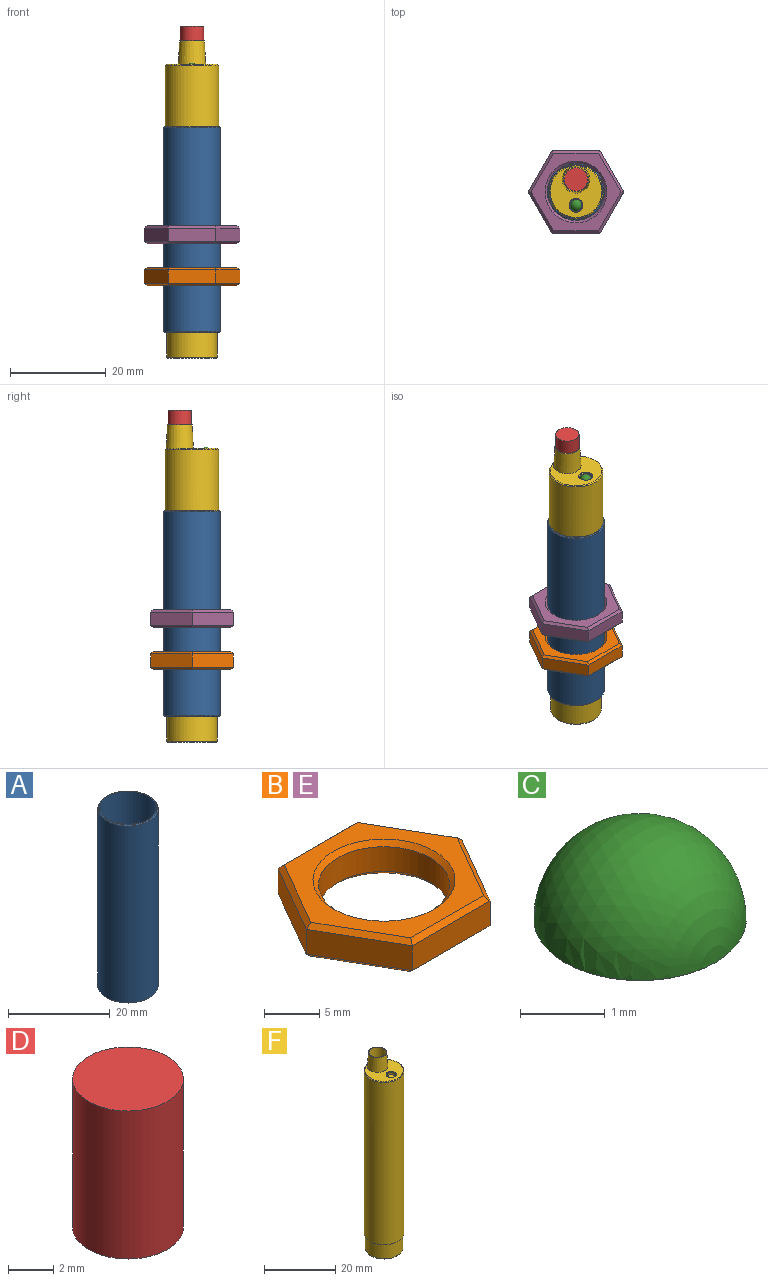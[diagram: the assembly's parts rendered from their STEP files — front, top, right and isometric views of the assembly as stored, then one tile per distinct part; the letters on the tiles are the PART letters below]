
ASSEMBLY  parts=6 mates=5
PART A: 6 faces, bbox 11.9x11.9x43 mm
  f0: plane 11.5x11.5mm, normal (0,0,-1), area 5.3mm2, adj f3,f4
  f1: plane 11.5x11.5mm, normal (0,0,1), area 5.3mm2, adj f3,f5
  f2: cylinder r=5.95mm len=42.6mm, axis (0,0,-1), area 1592.6mm2, adj f4,f5
  f3: cylinder r=5.6mm len=43mm, axis (0,0,-1), area 1513mm2, adj f0,f1
  f4: cone r=5.95mm half-angle=45deg, axis (0,0,1), area 10.4mm2, adj f0,f2
  f5: cone r=5.75mm half-angle=45deg, axis (0,0,-1), area 10.4mm2, adj f1,f2
PART B: 23 faces, bbox 19.9x17.3x3.8 mm
  f0: plane 8.63x4.98mm, normal (-0.87,0.5,0), area 27.4mm2, adj f1,f6,f14,f21
  f1: plane 8.63x4.98mm, normal (-0.87,-0.5,0), area 27.4mm2, adj f0,f2,f12,f19
  f2: plane 9.96x2.75mm, normal (0,-1,0), area 27.4mm2, adj f1,f3,f10,f17
  f3: plane 8.63x4.98mm, normal (0.87,-0.5,0), area 27.4mm2, adj f2,f4,f9,f16
  f4: plane 8.63x4.98mm, normal (0.87,0.5,0), area 27.4mm2, adj f3,f6,f11,f18
  f5: cylinder r=5.95mm len=11.9mm, axis (0,0,1), area 102.8mm2, adj f15,f22
  f6: plane 9.96x2.75mm, normal (0,1,0), area 27.4mm2, adj f0,f4,f13,f20
  f7: plane 18.76x16.25mm, normal (0,0,-1), area 98mm2, adj f9,f10,f11,f12,f13,f14,f15
  f8: plane 18.76x16.25mm, normal (0,0,1), area 98mm2, adj f16,f17,f18,f19,f20,f21,f22
  f9: plane 8.63x5.27mm, normal (0.61,-0.35,-0.71), area 6.8mm2, adj f3,f7,f10,f11
  f10: plane 9.96x0.5mm, normal (0,-0.71,-0.71), area 6.8mm2, adj f2,f7,f9,f12
  f11: plane 8.63x5.27mm, normal (0.61,0.35,-0.71), area 6.8mm2, adj f4,f7,f9,f13
  f12: plane 8.63x5.27mm, normal (-0.61,-0.35,-0.71), area 6.8mm2, adj f1,f7,f10,f14
  f13: plane 9.96x0.5mm, normal (0,0.71,-0.71), area 6.8mm2, adj f6,f7,f11,f14
  f14: plane 8.63x5.27mm, normal (-0.61,0.35,-0.71), area 6.8mm2, adj f0,f7,f12,f13
  f15: cone r=6.45mm half-angle=45deg, axis (0,0,-1), area 27.5mm2, adj f5,f7
  f16: plane 8.63x5.27mm, normal (0.61,-0.35,0.71), area 6.8mm2, adj f3,f8,f17,f18
  f17: plane 9.96x0.5mm, normal (0,-0.71,0.71), area 6.8mm2, adj f2,f8,f16,f19
  f18: plane 8.63x5.27mm, normal (0.61,0.35,0.71), area 6.8mm2, adj f4,f8,f16,f20
  f19: plane 8.63x5.27mm, normal (-0.61,-0.35,0.71), area 6.8mm2, adj f1,f8,f17,f21
  f20: plane 9.96x0.5mm, normal (0,0.71,0.71), area 6.8mm2, adj f6,f8,f18,f21
  f21: plane 8.63x5.27mm, normal (-0.61,0.35,0.71), area 6.8mm2, adj f0,f8,f19,f20
  f22: cone r=5.95mm half-angle=45deg, axis (0,0,1), area 27.5mm2, adj f5,f8
PART C: 2 faces, bbox 2.5x2.5x1.3 mm
  f0: sphere r=1.25mm, area 9.8mm2, adj f1
  f1: plane 2.5x2.5mm, normal (0,0,-1), area 4.9mm2, adj f0
PART D: 3 faces, bbox 4.9x4.9x8 mm
  f0: cylinder r=2.45mm len=8mm, axis (0,0,-1), area 123.2mm2, adj f1,f2
  f1: plane 4.9x4.9mm, normal (0,0,1), area 18.9mm2, adj f0
  f2: plane 4.9x4.9mm, normal (0,0,-1), area 18.9mm2, adj f0
PART E: same geometry as B
PART F: 14 faces, bbox 11.2x11.2x66.2 mm
  f0: cylinder r=5.6mm len=55.8mm, axis (0,0,-1), area 1963.4mm2, adj f3,f12
  f1: plane 10.8x10.8mm, normal (0,0,1), area 59.5mm2, adj f6,f11,f12
  f2: cylinder r=5.25mm len=10.5mm, axis (0,0,-1), area 168.2mm2, adj f3,f13
  f3: plane 11.2x11.2mm, normal (0,0,-1), area 11.9mm2, adj f0,f2
  f4: plane 10.1x10.1mm, normal (0,0,-1), area 80.1mm2, adj f13
  f5: cylinder r=2.45mm len=4.9mm, axis (0,0,-1), area 75.4mm2, adj f7,f8
  f6: cone r=2.85mm half-angle=3deg, axis (0,0,-1), area 83.9mm2, adj f1,f7
  f7: plane 5.19x5.19mm, normal (0,0,1), area 2.3mm2, adj f5,f6
  f8: plane 4.9x4.9mm, normal (0,0,1), area 18.9mm2, adj f5
  f9: cylinder r=1.25mm len=2.5mm, axis (0,0,1), area 6.3mm2, adj f10,f11
  f10: plane 2.5x2.5mm, normal (0,0,1), area 4.9mm2, adj f9
  f11: cone r=1.25mm half-angle=45deg, axis (0,0,1), area 2.4mm2, adj f1,f9
  f12: cone r=5.4mm half-angle=45deg, axis (0,0,-1), area 9.8mm2, adj f0,f1
  f13: cone r=5.25mm half-angle=45deg, axis (0,0,1), area 9.2mm2, adj f2,f4
PLACE A at identity
PLACE B t=(0,0,18.88)mm
PLACE C at identity
PLACE D at identity
PLACE E t=(0,0,27.63)mm
PLACE F at identity fixed
MATE slider F.f0 <-> B.f5  axis (0,0,-1) through (0,0,5.3)mm
MATE fastened D.f0 <-> F.f5  axis (0,0,-1) through (0,2.55,61.3)mm
MATE fastened C.f1 <-> F.f9  axis (0,0,-1) through (0,-2.85,60.3)mm
MATE fastened F.f0 <-> A.f2  axis (0,0,-1) through (0,0,5.3)mm
MATE fastened B.f5 <-> E.f5  axis (0,0,1) through (0,0,18.88)mm
